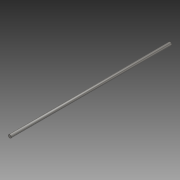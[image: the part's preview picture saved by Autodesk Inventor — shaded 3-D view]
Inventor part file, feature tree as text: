
AUTODESK INVENTOR PART (.ipt)
format: ipt  version: 2018 (Build 220112000, 112)  size: 76,288 bytes
history: native  units: mm
features: extrude x1, chamfer x1, sketch x1
ambient origin geometry x8: Origin, YZ Plane, XZ Plane, XY Plane, X Axis, Y Axis, Z Axis, Center Point
bodies: Solid1 (feature_tree)
feature tree (3):
  extrude  "Extrusion1"  Depth=500.0mm TaperAngle=0.0deg
  chamfer  "Chamfer1"  Distance=0.5mm Angle=45.0deg
  sketch  "Sketch1"  dims[d0=10.0mm d1=500.0mm d2=0.0mm d3=0.5mm d4=2.0mm d5=45.0deg]
